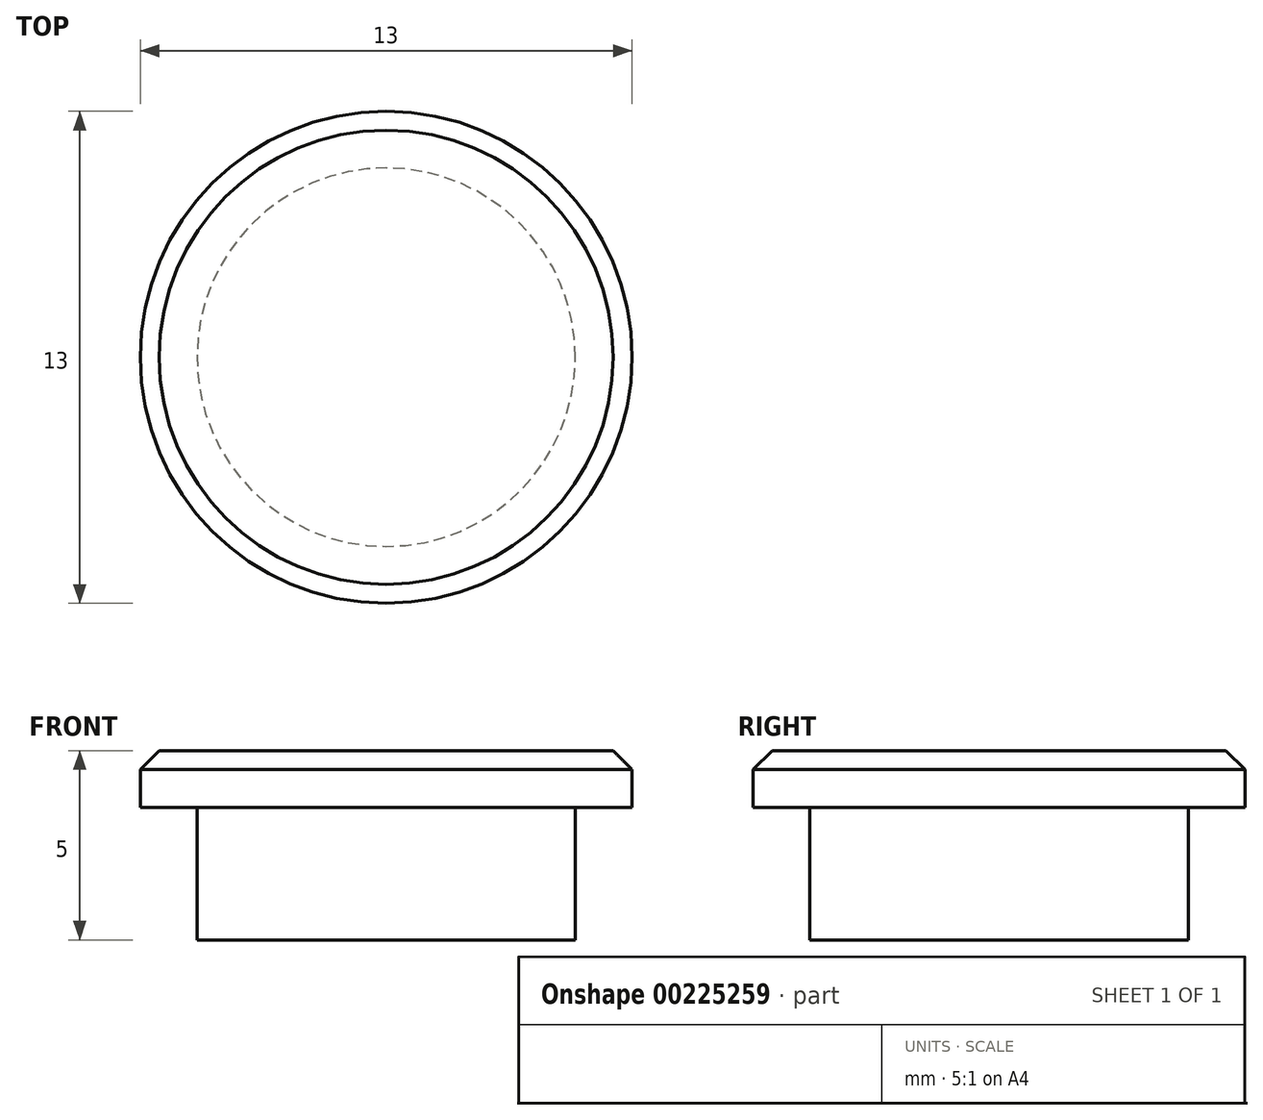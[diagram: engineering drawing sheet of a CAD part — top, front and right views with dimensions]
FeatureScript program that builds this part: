
annotation { "Feature Type Name" : "Feature", "Feature Type Description" : "" }
export const myFeature = defineFeature(function(context is Context, id is Id, definition is map)
    precondition{}
    {
        {
            var Q0;
            Q0=qCreatedBy(makeId("Top.planeOp"),FACE);
            var sketch = newSketch(context, id + "F0", { "sketchPlane" : qUnion([Q0])});
            skCircle(sketch, "E0", {"center": v(0, 0) * mm, "radius": 5 * mm});
            skSolve(sketch);
        }
        {
            var Q0;
            Q0=makeQuery(id+"F0.imprint","IMPRINT",FACE,{"disambiguationData":[TD([[makeQuery(id+"F0.imprint","IMPRINT",EDGE,{"derivedFrom":sQuery(id+"F0.wireOp",EDGE,"E0")}),1.0]])]});
            extrude(context, id + "F1", {"entities" : qUnion([Q0]), "depth" : 3.5 * mm});
        }
        {
            var Q0;
            Q0=makeQuery(id+"F1.opExtrude","CAP_FACE",FACE,{"disambiguationData":[OSD([sQuery(id+"F0.wireOp",EDGE,"E0")])],"isStart":false});
            var sketch = newSketch(context, id + "F2", { "sketchPlane" : qUnion([Q0])});
            skCircle(sketch, "E1", {"center": v(0, 0) * mm, "radius": 6.5 * mm});
            skSolve(sketch);
        }
        {
            var Q0;
            Q0 = qSketchRegion(id + "F2", true);
            extrude(context, id + "F3", {"entities" : qUnion([Q0]), "operationType" : NewBodyOperationType.ADD, "depth" : 1.5 * mm});
        }
        {
            var Q0;
            Q0=makeQuery(id+"F3.opExtrude","CAP_EDGE",EDGE,{"disambiguationData":[OSD([sQuery(id+"F2.wireOp",EDGE,"E1")])],"isStart":false});
            chamfer(context, id + "F4", {"entities" : qUnion([Q0]), "width" : 0.5 * mm, "tangentPropagation" : true});
        }
    });
